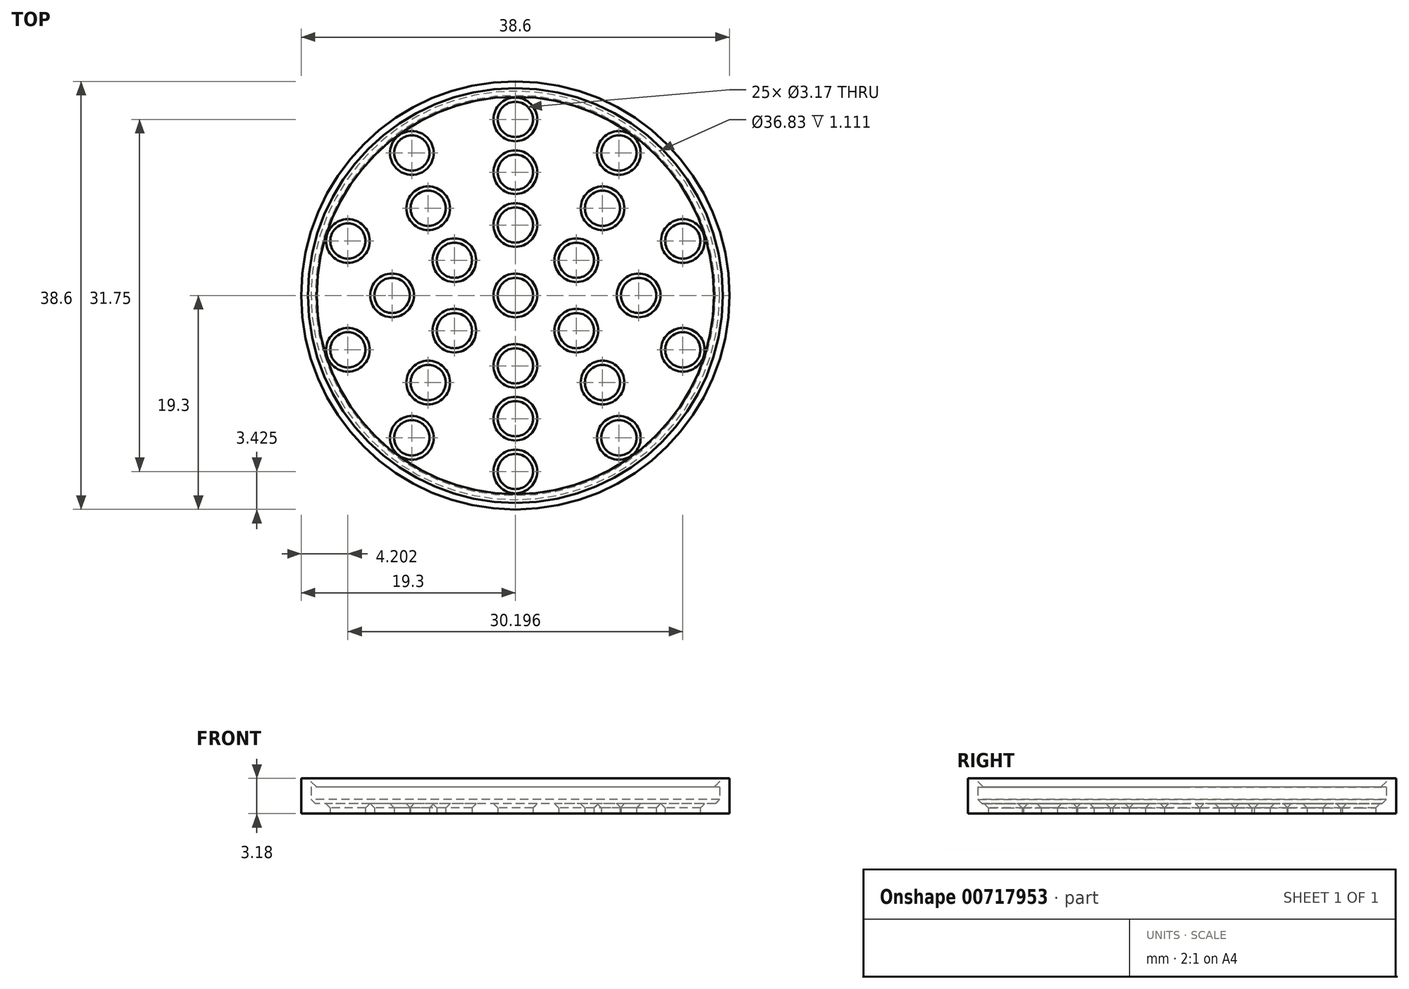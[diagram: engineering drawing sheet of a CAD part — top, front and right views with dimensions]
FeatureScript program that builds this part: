
annotation { "Feature Type Name" : "Feature", "Feature Type Description" : "" }
export const myFeature = defineFeature(function(context is Context, id is Id, definition is map)
    precondition{}
    {
        {
            var Q0;
            Q0=qCreatedBy(makeId("Top.planeOp"),FACE);
            var sketch = newSketch(context, id + "F0", { "sketchPlane" : qUnion([Q0])});
            skCircle(sketch, "E0", {"center": v(0, 0) * mm, "radius": 19.3 * mm});
            skCircle(sketch, "E1", {"center": v(0, 0) * mm, "radius": 6.35 * mm, "construction": true});
            skCircle(sketch, "E2", {"center": v(0, 0) * mm, "radius": 15.88 * mm, "construction": true});
            skCircle(sketch, "E3", {"center": v(0, 6.35) * mm, "radius": 1.59 * mm});
            skCircle(sketch, "E4", {"center": v(0, 15.88) * mm, "radius": 1.59 * mm});
            skCircle(sketch, "E5.1.0", {"center": v(-5.5, 3.18) * mm, "radius": 1.59 * mm});
            skCircle(sketch, "E5.2.0", {"center": v(-5.5, -3.17) * mm, "radius": 1.59 * mm});
            skCircle(sketch, "E5.3.0", {"center": v(0, -6.35) * mm, "radius": 1.59 * mm});
            skCircle(sketch, "E5.4.0", {"center": v(5.5, -3.18) * mm, "radius": 1.59 * mm});
            skCircle(sketch, "E5.5.0", {"center": v(5.5, 3.18) * mm, "radius": 1.59 * mm});
            skCircle(sketch, "E6", {"center": v(0, 0) * mm, "radius": 11.11 * mm, "construction": true});
            skCircle(sketch, "E7", {"center": v(0, 11.11) * mm, "radius": 1.59 * mm});
            skCircle(sketch, "E8.1.0", {"center": v(-7.86, 7.86) * mm, "radius": 1.59 * mm});
            skCircle(sketch, "E8.2.0", {"center": v(-11.11, 0) * mm, "radius": 1.59 * mm});
            skCircle(sketch, "E8.3.0", {"center": v(-7.86, -7.86) * mm, "radius": 1.59 * mm});
            skCircle(sketch, "E8.4.0", {"center": v(0, -11.11) * mm, "radius": 1.59 * mm});
            skCircle(sketch, "E8.5.0", {"center": v(7.86, -7.86) * mm, "radius": 1.59 * mm});
            skCircle(sketch, "E8.6.0", {"center": v(11.11, 0) * mm, "radius": 1.59 * mm});
            skCircle(sketch, "E8.7.0", {"center": v(7.86, 7.86) * mm, "radius": 1.59 * mm});
            skCircle(sketch, "E9.1.0", {"center": v(-9.33, 12.84) * mm, "radius": 1.59 * mm});
            skCircle(sketch, "E9.2.0", {"center": v(-15.1, 4.9) * mm, "radius": 1.59 * mm});
            skCircle(sketch, "E9.3.0", {"center": v(-15.1, -4.9) * mm, "radius": 1.59 * mm});
            skCircle(sketch, "E9.4.0", {"center": v(-9.33, -12.84) * mm, "radius": 1.59 * mm});
            skCircle(sketch, "E9.5.0", {"center": v(0, -15.88) * mm, "radius": 1.59 * mm});
            skCircle(sketch, "E9.6.0", {"center": v(9.33, -12.84) * mm, "radius": 1.59 * mm});
            skCircle(sketch, "E9.7.0", {"center": v(15.1, -4.9) * mm, "radius": 1.59 * mm});
            skCircle(sketch, "E9.8.0", {"center": v(15.1, 4.9) * mm, "radius": 1.59 * mm});
            skCircle(sketch, "E9.9.0", {"center": v(9.33, 12.84) * mm, "radius": 1.59 * mm});
            skCircle(sketch, "E10", {"center": v(0, 0) * mm, "radius": 1.59 * mm});
            skSolve(sketch);
        }
        {
            var Q0;
            Q0=makeQuery(id+"F0.imprint","IMPRINT",FACE,{"disambiguationData":[TD([[makeQuery(id+"F0.imprint","IMPRINT",EDGE,{"derivedFrom":sQuery(id+"F0.wireOp",EDGE,"E0")}),1.0]])]});
            var Q1;
            Q1=makeQuery(id+"F0.imprint","IMPRINT",FACE,{"disambiguationData":[TD([[makeQuery(id+"F0.imprint","IMPRINT",EDGE,{"derivedFrom":sQuery(id+"F0.wireOp",EDGE,"E10")}),1.0]])]});
            var Q2;
            Q2=makeQuery(id+"F0.imprint","IMPRINT",FACE,{"disambiguationData":[TD([[makeQuery(id+"F0.imprint","IMPRINT",EDGE,{"derivedFrom":sQuery(id+"F0.wireOp",EDGE,"E5.5.0")}),1.0]])]});
            var Q3;
            Q3=makeQuery(id+"F0.imprint","IMPRINT",FACE,{"disambiguationData":[TD([[makeQuery(id+"F0.imprint","IMPRINT",EDGE,{"derivedFrom":sQuery(id+"F0.wireOp",EDGE,"E8.8.0")}),1.0]])]});
            var Q4;
            Q4=makeQuery(id+"F0.imprint","IMPRINT",FACE,{"disambiguationData":[TD([[makeQuery(id+"F0.imprint","IMPRINT",EDGE,{"derivedFrom":sQuery(id+"F0.wireOp",EDGE,"E9.10.0")}),1.0]])]});
            var Q5;
            Q5=makeQuery(id+"F0.imprint","IMPRINT",FACE,{"disambiguationData":[TD([[makeQuery(id+"F0.imprint","IMPRINT",EDGE,{"derivedFrom":sQuery(id+"F0.wireOp",EDGE,"E8.9.0")}),1.0]])]});
            var Q6;
            Q6=makeQuery(id+"F0.imprint","IMPRINT",FACE,{"disambiguationData":[TD([[makeQuery(id+"F0.imprint","IMPRINT",EDGE,{"derivedFrom":sQuery(id+"F0.wireOp",EDGE,"E9.11.0")}),1.0]])]});
            var Q7;
            Q7=makeQuery(id+"F0.imprint","IMPRINT",FACE,{"disambiguationData":[TD([[makeQuery(id+"F0.imprint","IMPRINT",EDGE,{"derivedFrom":sQuery(id+"F0.wireOp",EDGE,"E4")}),1.0]])]});
            var Q8;
            Q8=makeQuery(id+"F0.imprint","IMPRINT",FACE,{"disambiguationData":[TD([[makeQuery(id+"F0.imprint","IMPRINT",EDGE,{"derivedFrom":sQuery(id+"F0.wireOp",EDGE,"E7")}),1.0]])]});
            var Q9;
            Q9=makeQuery(id+"F0.imprint","IMPRINT",FACE,{"disambiguationData":[TD([[makeQuery(id+"F0.imprint","IMPRINT",EDGE,{"derivedFrom":sQuery(id+"F0.wireOp",EDGE,"E3")}),1.0]])]});
            var Q10;
            Q10=makeQuery(id+"F0.imprint","IMPRINT",FACE,{"disambiguationData":[TD([[makeQuery(id+"F0.imprint","IMPRINT",EDGE,{"derivedFrom":sQuery(id+"F0.wireOp",EDGE,"E9.1.0")}),1.0]])]});
            var Q11;
            Q11=makeQuery(id+"F0.imprint","IMPRINT",FACE,{"disambiguationData":[TD([[makeQuery(id+"F0.imprint","IMPRINT",EDGE,{"derivedFrom":sQuery(id+"F0.wireOp",EDGE,"E8.1.0")}),1.0]])]});
            var Q12;
            Q12=makeQuery(id+"F0.imprint","IMPRINT",FACE,{"disambiguationData":[TD([[makeQuery(id+"F0.imprint","IMPRINT",EDGE,{"derivedFrom":sQuery(id+"F0.wireOp",EDGE,"E9.2.0")}),1.0]])]});
            var Q13;
            Q13=makeQuery(id+"F0.imprint","IMPRINT",FACE,{"disambiguationData":[TD([[makeQuery(id+"F0.imprint","IMPRINT",EDGE,{"derivedFrom":sQuery(id+"F0.wireOp",EDGE,"E8.2.0")}),1.0]])]});
            var Q14;
            Q14=makeQuery(id+"F0.imprint","IMPRINT",FACE,{"disambiguationData":[TD([[makeQuery(id+"F0.imprint","IMPRINT",EDGE,{"derivedFrom":sQuery(id+"F0.wireOp",EDGE,"E5.1.0")}),1.0]])]});
            var Q15;
            Q15=makeQuery(id+"F0.imprint","IMPRINT",FACE,{"disambiguationData":[TD([[makeQuery(id+"F0.imprint","IMPRINT",EDGE,{"derivedFrom":sQuery(id+"F0.wireOp",EDGE,"E9.3.0")}),1.0]])]});
            var Q16;
            Q16=makeQuery(id+"F0.imprint","IMPRINT",FACE,{"disambiguationData":[TD([[makeQuery(id+"F0.imprint","IMPRINT",EDGE,{"derivedFrom":sQuery(id+"F0.wireOp",EDGE,"E8.3.0")}),1.0]])]});
            var Q17;
            Q17=makeQuery(id+"F0.imprint","IMPRINT",FACE,{"disambiguationData":[TD([[makeQuery(id+"F0.imprint","IMPRINT",EDGE,{"derivedFrom":sQuery(id+"F0.wireOp",EDGE,"E5.2.0")}),1.0]])]});
            var Q18;
            Q18=makeQuery(id+"F0.imprint","IMPRINT",FACE,{"disambiguationData":[TD([[makeQuery(id+"F0.imprint","IMPRINT",EDGE,{"derivedFrom":sQuery(id+"F0.wireOp",EDGE,"E9.4.0")}),1.0]])]});
            var Q19;
            Q19=makeQuery(id+"F0.imprint","IMPRINT",FACE,{"disambiguationData":[TD([[makeQuery(id+"F0.imprint","IMPRINT",EDGE,{"derivedFrom":sQuery(id+"F0.wireOp",EDGE,"E8.4.0")}),1.0]])]});
            var Q20;
            Q20=makeQuery(id+"F0.imprint","IMPRINT",FACE,{"disambiguationData":[TD([[makeQuery(id+"F0.imprint","IMPRINT",EDGE,{"derivedFrom":sQuery(id+"F0.wireOp",EDGE,"E9.5.0")}),1.0]])]});
            var Q21;
            Q21=makeQuery(id+"F0.imprint","IMPRINT",FACE,{"disambiguationData":[TD([[makeQuery(id+"F0.imprint","IMPRINT",EDGE,{"derivedFrom":sQuery(id+"F0.wireOp",EDGE,"E5.3.0")}),1.0]])]});
            var Q22;
            Q22=makeQuery(id+"F0.imprint","IMPRINT",FACE,{"disambiguationData":[TD([[makeQuery(id+"F0.imprint","IMPRINT",EDGE,{"derivedFrom":sQuery(id+"F0.wireOp",EDGE,"E8.5.0")}),1.0]])]});
            var Q23;
            Q23=makeQuery(id+"F0.imprint","IMPRINT",FACE,{"disambiguationData":[TD([[makeQuery(id+"F0.imprint","IMPRINT",EDGE,{"derivedFrom":sQuery(id+"F0.wireOp",EDGE,"E9.6.0")}),1.0]])]});
            var Q24;
            Q24=makeQuery(id+"F0.imprint","IMPRINT",FACE,{"disambiguationData":[TD([[makeQuery(id+"F0.imprint","IMPRINT",EDGE,{"derivedFrom":sQuery(id+"F0.wireOp",EDGE,"E9.7.0")}),1.0]])]});
            var Q25;
            Q25=makeQuery(id+"F0.imprint","IMPRINT",FACE,{"disambiguationData":[TD([[makeQuery(id+"F0.imprint","IMPRINT",EDGE,{"derivedFrom":sQuery(id+"F0.wireOp",EDGE,"E8.6.0")}),1.0]])]});
            var Q26;
            Q26=makeQuery(id+"F0.imprint","IMPRINT",FACE,{"disambiguationData":[TD([[makeQuery(id+"F0.imprint","IMPRINT",EDGE,{"derivedFrom":sQuery(id+"F0.wireOp",EDGE,"E5.4.0")}),1.0]])]});
            var Q27;
            Q27=makeQuery(id+"F0.imprint","IMPRINT",FACE,{"disambiguationData":[TD([[makeQuery(id+"F0.imprint","IMPRINT",EDGE,{"derivedFrom":sQuery(id+"F0.wireOp",EDGE,"E8.7.0")}),1.0]])]});
            var Q28;
            Q28=makeQuery(id+"F0.imprint","IMPRINT",FACE,{"disambiguationData":[TD([[makeQuery(id+"F0.imprint","IMPRINT",EDGE,{"derivedFrom":sQuery(id+"F0.wireOp",EDGE,"E9.8.0")}),1.0]])]});
            var Q29;
            Q29=makeQuery(id+"F0.imprint","IMPRINT",FACE,{"disambiguationData":[TD([[makeQuery(id+"F0.imprint","IMPRINT",EDGE,{"derivedFrom":sQuery(id+"F0.wireOp",EDGE,"E9.9.0")}),1.0]])]});
            extrude(context, id + "F1", {"entities" : qUnion([Q0, Q1, Q2, Q3, Q4, Q5, Q6, Q7, Q8, Q9, Q10, Q11, Q12, Q13, Q14, Q15, Q16, Q17, Q18, Q19, Q20, Q21, Q22, Q23, Q24, Q25, Q26, Q27, Q28, Q29]), "depth" : 3.17 * mm, "offsetDistance" : 25.4 * mm});
        }
        {
            var Q0;
            Q0=makeQuery(id+"F1.opExtrude","CAP_FACE",FACE,{"disambiguationData":[OSD([sQuery(id+"F0.wireOp",EDGE,"E0")])],"isStart":false});
            shell(context, id + "F2", {"entities" : qUnion([Q0]), "thickness" : 0.89 * mm});
        }
        {
            var Q0;
            Q0=makeQuery(id+"F0.imprint","IMPRINT",FACE,{"disambiguationData":[TD([[makeQuery(id+"F0.imprint","IMPRINT",EDGE,{"derivedFrom":sQuery(id+"F0.wireOp",EDGE,"E5.3.0")}),1.0]])]});
            var Q1;
            Q1=makeQuery(id+"F0.imprint","IMPRINT",FACE,{"disambiguationData":[TD([[makeQuery(id+"F0.imprint","IMPRINT",EDGE,{"derivedFrom":sQuery(id+"F0.wireOp",EDGE,"E8.5.0")}),1.0]])]});
            var Q2;
            Q2=makeQuery(id+"F0.imprint","IMPRINT",FACE,{"disambiguationData":[TD([[makeQuery(id+"F0.imprint","IMPRINT",EDGE,{"derivedFrom":sQuery(id+"F0.wireOp",EDGE,"E9.6.0")}),1.0]])]});
            var Q3;
            Q3=makeQuery(id+"F0.imprint","IMPRINT",FACE,{"disambiguationData":[TD([[makeQuery(id+"F0.imprint","IMPRINT",EDGE,{"derivedFrom":sQuery(id+"F0.wireOp",EDGE,"E8.4.0")}),1.0]])]});
            var Q4;
            Q4=makeQuery(id+"F0.imprint","IMPRINT",FACE,{"disambiguationData":[TD([[makeQuery(id+"F0.imprint","IMPRINT",EDGE,{"derivedFrom":sQuery(id+"F0.wireOp",EDGE,"E9.5.0")}),1.0]])]});
            var Q5;
            Q5=makeQuery(id+"F0.imprint","IMPRINT",FACE,{"disambiguationData":[TD([[makeQuery(id+"F0.imprint","IMPRINT",EDGE,{"derivedFrom":sQuery(id+"F0.wireOp",EDGE,"E9.4.0")}),1.0]])]});
            var Q6;
            Q6=makeQuery(id+"F0.imprint","IMPRINT",FACE,{"disambiguationData":[TD([[makeQuery(id+"F0.imprint","IMPRINT",EDGE,{"derivedFrom":sQuery(id+"F0.wireOp",EDGE,"E8.3.0")}),1.0]])]});
            var Q7;
            Q7=makeQuery(id+"F0.imprint","IMPRINT",FACE,{"disambiguationData":[TD([[makeQuery(id+"F0.imprint","IMPRINT",EDGE,{"derivedFrom":sQuery(id+"F0.wireOp",EDGE,"E5.2.0")}),1.0]])]});
            var Q8;
            Q8=makeQuery(id+"F0.imprint","IMPRINT",FACE,{"disambiguationData":[TD([[makeQuery(id+"F0.imprint","IMPRINT",EDGE,{"derivedFrom":sQuery(id+"F0.wireOp",EDGE,"E9.3.0")}),1.0]])]});
            var Q9;
            Q9=makeQuery(id+"F0.imprint","IMPRINT",FACE,{"disambiguationData":[TD([[makeQuery(id+"F0.imprint","IMPRINT",EDGE,{"derivedFrom":sQuery(id+"F0.wireOp",EDGE,"E8.2.0")}),1.0]])]});
            var Q10;
            Q10=makeQuery(id+"F0.imprint","IMPRINT",FACE,{"disambiguationData":[TD([[makeQuery(id+"F0.imprint","IMPRINT",EDGE,{"derivedFrom":sQuery(id+"F0.wireOp",EDGE,"E5.1.0")}),1.0]])]});
            var Q11;
            Q11=makeQuery(id+"F0.imprint","IMPRINT",FACE,{"disambiguationData":[TD([[makeQuery(id+"F0.imprint","IMPRINT",EDGE,{"derivedFrom":sQuery(id+"F0.wireOp",EDGE,"E9.2.0")}),1.0]])]});
            var Q12;
            Q12=makeQuery(id+"F0.imprint","IMPRINT",FACE,{"disambiguationData":[TD([[makeQuery(id+"F0.imprint","IMPRINT",EDGE,{"derivedFrom":sQuery(id+"F0.wireOp",EDGE,"E9.1.0")}),1.0]])]});
            var Q13;
            Q13=makeQuery(id+"F0.imprint","IMPRINT",FACE,{"disambiguationData":[TD([[makeQuery(id+"F0.imprint","IMPRINT",EDGE,{"derivedFrom":sQuery(id+"F0.wireOp",EDGE,"E8.1.0")}),1.0]])]});
            var Q14;
            Q14=makeQuery(id+"F0.imprint","IMPRINT",FACE,{"disambiguationData":[TD([[makeQuery(id+"F0.imprint","IMPRINT",EDGE,{"derivedFrom":sQuery(id+"F0.wireOp",EDGE,"E4")}),1.0]])]});
            var Q15;
            Q15=makeQuery(id+"F0.imprint","IMPRINT",FACE,{"disambiguationData":[TD([[makeQuery(id+"F0.imprint","IMPRINT",EDGE,{"derivedFrom":sQuery(id+"F0.wireOp",EDGE,"E7")}),1.0]])]});
            var Q16;
            Q16=makeQuery(id+"F0.imprint","IMPRINT",FACE,{"disambiguationData":[TD([[makeQuery(id+"F0.imprint","IMPRINT",EDGE,{"derivedFrom":sQuery(id+"F0.wireOp",EDGE,"E3")}),1.0]])]});
            var Q17;
            Q17=makeQuery(id+"F0.imprint","IMPRINT",FACE,{"disambiguationData":[TD([[makeQuery(id+"F0.imprint","IMPRINT",EDGE,{"derivedFrom":sQuery(id+"F0.wireOp",EDGE,"E9.11.0")}),1.0]])]});
            var Q18;
            Q18=makeQuery(id+"F0.imprint","IMPRINT",FACE,{"disambiguationData":[TD([[makeQuery(id+"F0.imprint","IMPRINT",EDGE,{"derivedFrom":sQuery(id+"F0.wireOp",EDGE,"E8.9.0")}),1.0]])]});
            var Q19;
            Q19=makeQuery(id+"F0.imprint","IMPRINT",FACE,{"disambiguationData":[TD([[makeQuery(id+"F0.imprint","IMPRINT",EDGE,{"derivedFrom":sQuery(id+"F0.wireOp",EDGE,"E5.5.0")}),1.0]])]});
            var Q20;
            Q20=makeQuery(id+"F0.imprint","IMPRINT",FACE,{"disambiguationData":[TD([[makeQuery(id+"F0.imprint","IMPRINT",EDGE,{"derivedFrom":sQuery(id+"F0.wireOp",EDGE,"E9.10.0")}),1.0]])]});
            var Q21;
            Q21=makeQuery(id+"F0.imprint","IMPRINT",FACE,{"disambiguationData":[TD([[makeQuery(id+"F0.imprint","IMPRINT",EDGE,{"derivedFrom":sQuery(id+"F0.wireOp",EDGE,"E8.8.0")}),1.0]])]});
            var Q22;
            Q22=makeQuery(id+"F0.imprint","IMPRINT",FACE,{"disambiguationData":[TD([[makeQuery(id+"F0.imprint","IMPRINT",EDGE,{"derivedFrom":sQuery(id+"F0.wireOp",EDGE,"E9.9.0")}),1.0]])]});
            var Q23;
            Q23=makeQuery(id+"F0.imprint","IMPRINT",FACE,{"disambiguationData":[TD([[makeQuery(id+"F0.imprint","IMPRINT",EDGE,{"derivedFrom":sQuery(id+"F0.wireOp",EDGE,"E8.7.0")}),1.0]])]});
            var Q24;
            Q24=makeQuery(id+"F0.imprint","IMPRINT",FACE,{"disambiguationData":[TD([[makeQuery(id+"F0.imprint","IMPRINT",EDGE,{"derivedFrom":sQuery(id+"F0.wireOp",EDGE,"E5.4.0")}),1.0]])]});
            var Q25;
            Q25=makeQuery(id+"F0.imprint","IMPRINT",FACE,{"disambiguationData":[TD([[makeQuery(id+"F0.imprint","IMPRINT",EDGE,{"derivedFrom":sQuery(id+"F0.wireOp",EDGE,"E9.8.0")}),1.0]])]});
            var Q26;
            Q26=makeQuery(id+"F0.imprint","IMPRINT",FACE,{"disambiguationData":[TD([[makeQuery(id+"F0.imprint","IMPRINT",EDGE,{"derivedFrom":sQuery(id+"F0.wireOp",EDGE,"E9.7.0")}),1.0]])]});
            var Q27;
            Q27=makeQuery(id+"F0.imprint","IMPRINT",FACE,{"disambiguationData":[TD([[makeQuery(id+"F0.imprint","IMPRINT",EDGE,{"derivedFrom":sQuery(id+"F0.wireOp",EDGE,"E8.6.0")}),1.0]])]});
            var Q28;
            Q28=makeQuery(id+"F0.imprint","IMPRINT",FACE,{"disambiguationData":[TD([[makeQuery(id+"F0.imprint","IMPRINT",EDGE,{"derivedFrom":sQuery(id+"F0.wireOp",EDGE,"E10")}),1.0]])]});
            extrude(context, id + "F3", {"entities" : qUnion([Q0, Q1, Q2, Q3, Q4, Q5, Q6, Q7, Q8, Q9, Q10, Q11, Q12, Q13, Q14, Q15, Q16, Q17, Q18, Q19, Q20, Q21, Q22, Q23, Q24, Q25, Q26, Q27, Q28]), "operationType" : NewBodyOperationType.REMOVE, "endBound" : BoundingType.THROUGH_ALL, "depth" : 25.4 * mm, "offsetDistance" : 25.4 * mm});
        }
        {
            var Q0;
            Q0=makeQuery(id+"F1.opExtrude","CAP_FACE",FACE,{"disambiguationData":[OSD([sQuery(id+"F0.wireOp",EDGE,"E0")])],"isStart":false});
            var sketch = newSketch(context, id + "F4", { "sketchPlane" : qUnion([Q0])});
            skCircle(sketch, "E11", {"center": v(0, 0) * mm, "radius": 17.9 * mm});
            skSolve(sketch);
        }
        {
            var Q0;
            Q0=makeQuery(id+"F4.imprint","IMPRINT",FACE,{"disambiguationData":[TD([[makeQuery(id+"F4.imprint","IMPRINT",EDGE,{"derivedFrom":sQuery(id+"F4.wireOp",EDGE,"E11")}),-1.0]])]});
            extrude(context, id + "F5", {"entities" : qUnion([Q0]), "operationType" : NewBodyOperationType.ADD, "oppositeDirection" : true, "depth" : 0.8 * mm, "offsetDistance" : 25.4 * mm});
        }
        {
            var Q0;
            Q0=makeQuery(id+"F5.opExtrude","CAP_EDGE",EDGE,{"disambiguationData":[OSD([sQuery(id+"F4.wireOp",EDGE,"E11")])],"isStart":true});
            chamfer(context, id + "F6", {"entities" : qUnion([Q0]), "width" : 0.8 * mm, "tangentPropagation" : true});
        }
        {
            var Q0;
            {var subQ0=sQuery(id+"F0.wireOp",EDGE,"E0");Q0=makeQuery(id+"F2.opShell","OFFSET_FACE",FACE,{"disambiguationData":[OSD([subQ0]),TDD([makeQuery(id+"F1.opExtrude","CAP_FACE",FACE,{"disambiguationData":[OSD([subQ0])],"isStart":true})])]});}
            chamfer(context, id + "F7", {"entities" : qUnion([Q0]), "width" : 0.38 * mm, "tangentPropagation" : true});
        }
    });
